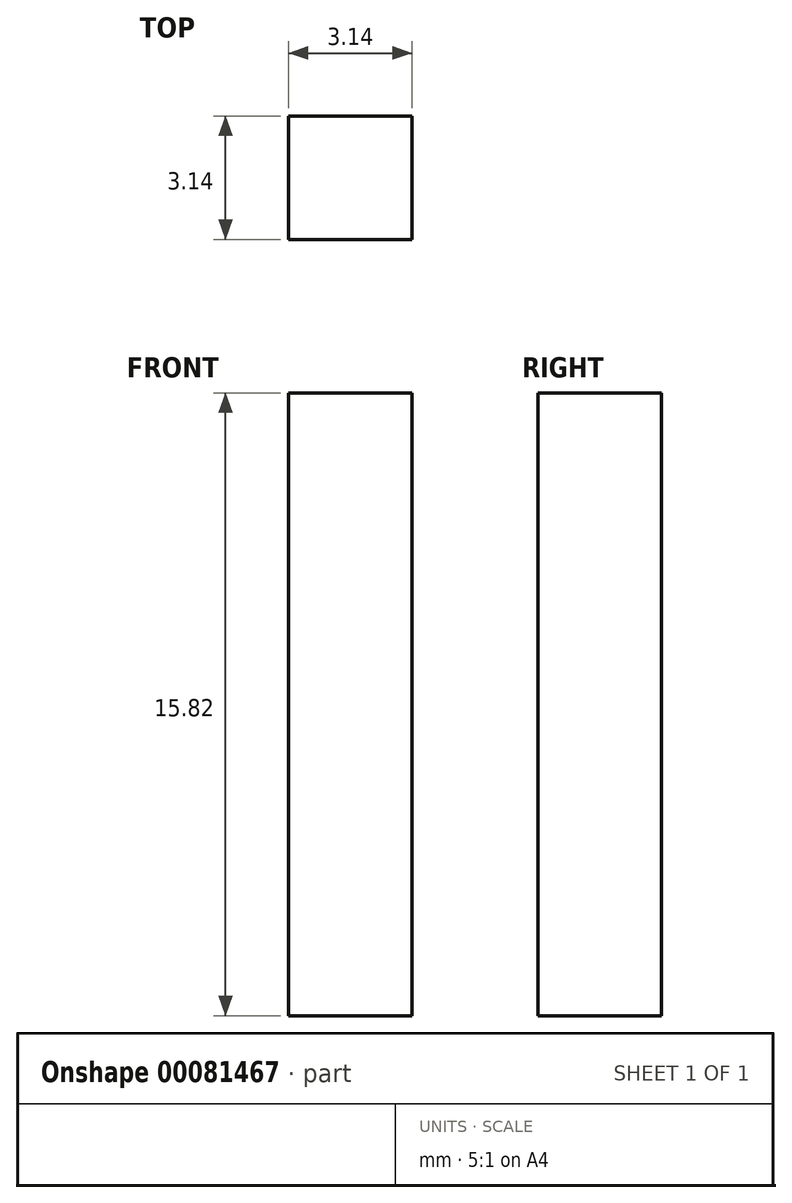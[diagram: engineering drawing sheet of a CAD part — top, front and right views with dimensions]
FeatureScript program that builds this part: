
annotation { "Feature Type Name" : "Feature", "Feature Type Description" : "" }
export const myFeature = defineFeature(function(context is Context, id is Id, definition is map)
    precondition{}
    {
        {
            var Q0;
            Q0=qCreatedBy(makeId("Top.planeOp"),FACE);
            var sketch = newSketch(context, id + "F0", { "sketchPlane" : qUnion([Q0])});
            skLineSegment(sketch, "E0.bottom", {"start": v(-4.4, 3.4) * mm, "end": v(-1.25, 3.4) * mm});
            skLineSegment(sketch, "E0.top", {"start": v(-4.4, 0.27) * mm, "end": v(-1.25, 0.27) * mm});
            skLineSegment(sketch, "E0.left", {"start": v(-4.4, 3.4) * mm, "end": v(-4.4, 0.27) * mm});
            skLineSegment(sketch, "E0.right", {"start": v(-1.25, 3.4) * mm, "end": v(-1.25, 0.27) * mm});
            skSolve(sketch);
        }
        {
            var Q0;
            Q0 = qSketchRegion(id + "F0", true);
            extrude(context, id + "F1", {"entities" : qUnion([Q0]), "depth" : 15.82 * mm});
        }
    });
